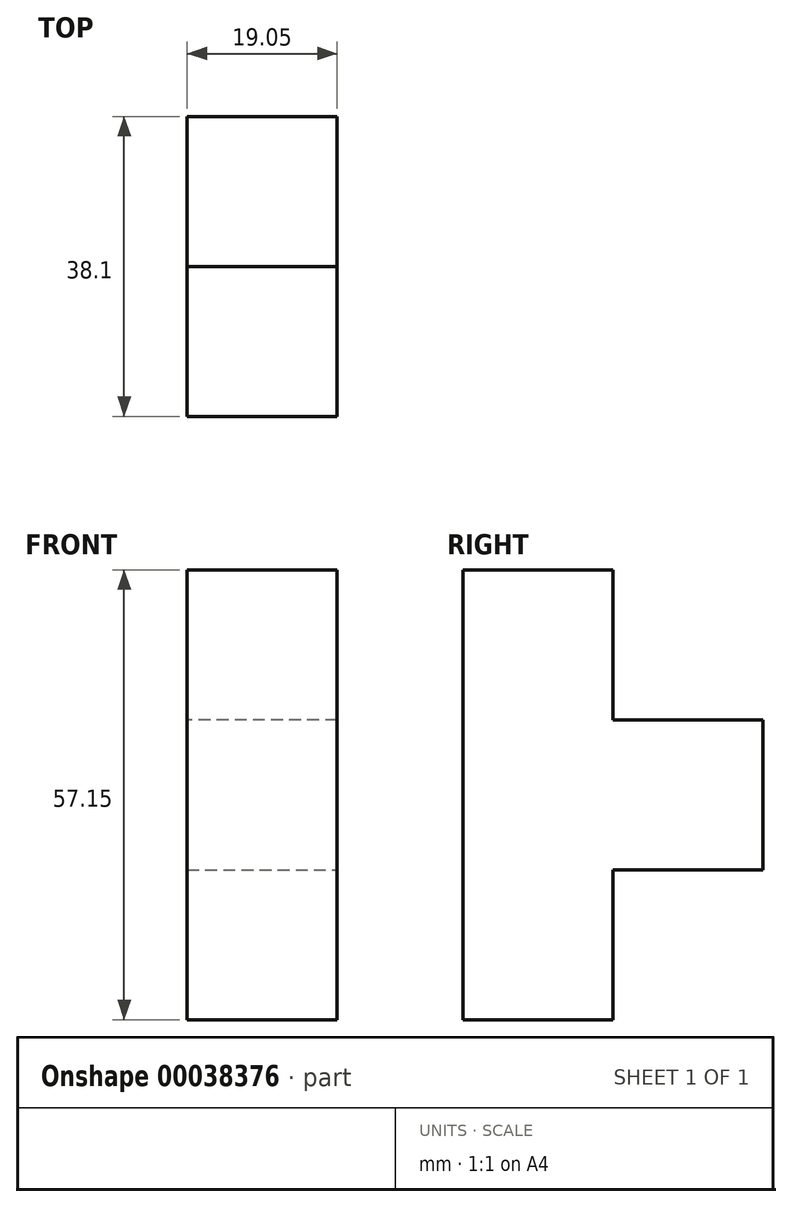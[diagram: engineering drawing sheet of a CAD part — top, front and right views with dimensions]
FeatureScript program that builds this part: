
annotation { "Feature Type Name" : "Feature", "Feature Type Description" : "" }
export const myFeature = defineFeature(function(context is Context, id is Id, definition is map)
    precondition{}
    {
        {
            var Q0;
            Q0=qCreatedBy(makeId("Top.planeOp"),FACE);
            var sketch = newSketch(context, id + "F0", { "sketchPlane" : qUnion([Q0])});
            skLineSegment(sketch, "E0.bottom", {"start": v(0, 0) * mm, "end": v(19.05, 0) * mm});
            skLineSegment(sketch, "E0.top", {"start": v(0, 19.05) * mm, "end": v(19.05, 19.05) * mm});
            skLineSegment(sketch, "E0.left", {"start": v(0, 0) * mm, "end": v(0, 19.05) * mm});
            skLineSegment(sketch, "E0.right", {"start": v(19.05, 0) * mm, "end": v(19.05, 19.05) * mm});
            skSolve(sketch);
        }
        {
            var Q0;
            Q0=makeQuery(id+"F0.imprint","IMPRINT",FACE,{"disambiguationData":[TD([[makeQuery(id+"F0.imprint","IMPRINT",EDGE,{"derivedFrom":sQuery(id+"F0.wireOp",EDGE,"E0.bottom")}),1.0]])]});
            extrude(context, id + "F1", {"entities" : qUnion([Q0]), "depth" : 19.05 * mm});
        }
        {
            var Q0;
            Q0=makeQuery(id+"F1.opExtrude","CAP_FACE",FACE,{"disambiguationData":[OSD([sQuery(id+"F0.wireOp",EDGE,"E0.bottom"),sQuery(id+"F0.wireOp",EDGE,"E0.top"),sQuery(id+"F0.wireOp",EDGE,"E0.left"),sQuery(id+"F0.wireOp",EDGE,"E0.right")])],"isStart":false});
            extrude(context, id + "F2", {"entities" : qUnion([Q0]), "operationType" : NewBodyOperationType.ADD, "depth" : 19.05 * mm});
        }
        {
            var Q0;
            {var subQ0=sQuery(id+"F0.wireOp",EDGE,"E0.top");Q0=makeQuery(id+"F2.boolean.opBoolean","MERGE",FACE,{"derivedFrom":[makeQuery(id+"F1.opExtrude","SWEPT_FACE",FACE,{"disambiguationData":[OSD([subQ0])]}),makeQuery(id+"F2.opExtrude","SWEPT_FACE",FACE,{"disambiguationData":[OSD([subQ0])]})]});}
            var sketch = newSketch(context, id + "F3", { "sketchPlane" : qUnion([Q0])});
            skLineSegment(sketch, "E1.bottom", {"start": v(0, 19.05) * mm, "end": v(-19.05, 19.05) * mm});
            skLineSegment(sketch, "E1.top", {"start": v(0, 38.1) * mm, "end": v(-19.05, 38.1) * mm});
            skLineSegment(sketch, "E1.left", {"start": v(0, 19.05) * mm, "end": v(0, 38.1) * mm});
            skLineSegment(sketch, "E1.right", {"start": v(-19.05, 19.05) * mm, "end": v(-19.05, 38.1) * mm});
            skSolve(sketch);
        }
        {
            var Q0;
            Q0=makeQuery(id+"F3.imprint","IMPRINT",FACE,{"disambiguationData":[TD([[makeQuery(id+"F3.imprint","IMPRINT",EDGE,{"derivedFrom":sQuery(id+"F3.wireOp",EDGE,"E1.bottom")}),-1.0]])]});
            extrude(context, id + "F4", {"entities" : qUnion([Q0]), "operationType" : NewBodyOperationType.ADD, "depth" : 19.05 * mm});
        }
        {
            var Q0;
            Q0=makeQuery(id+"F4.boolean.opBoolean","MERGE",FACE,{"derivedFrom":[makeQuery(id+"F2.opExtrude","CAP_FACE",FACE,{"disambiguationData":[OSD([sQuery(id+"F0.wireOp",EDGE,"E0.bottom"),sQuery(id+"F0.wireOp",EDGE,"E0.top"),sQuery(id+"F0.wireOp",EDGE,"E0.left"),sQuery(id+"F0.wireOp",EDGE,"E0.right")])],"isStart":false}),makeQuery(id+"F4.opExtrude","SWEPT_FACE",FACE,{"disambiguationData":[OSD([sQuery(id+"F3.wireOp",EDGE,"E1.top")])]})]});
            var sketch = newSketch(context, id + "F5", { "sketchPlane" : qUnion([Q0])});
            skLineSegment(sketch, "E2.bottom", {"start": v(19.05, 19.05) * mm, "end": v(0, 19.05) * mm});
            skLineSegment(sketch, "E2.top", {"start": v(19.05, 0) * mm, "end": v(0, 0) * mm});
            skLineSegment(sketch, "E2.left", {"start": v(19.05, 19.05) * mm, "end": v(19.05, 0) * mm});
            skLineSegment(sketch, "E2.right", {"start": v(0, 19.05) * mm, "end": v(0, 0) * mm});
            skSolve(sketch);
        }
        {
            var Q0;
            Q0=makeQuery(id+"F5.imprint","IMPRINT",FACE,{"disambiguationData":[TD([[makeQuery(id+"F5.imprint","IMPRINT",EDGE,{"derivedFrom":sQuery(id+"F5.wireOp",EDGE,"E2.bottom")}),1.0]])]});
            extrude(context, id + "F6", {"entities" : qUnion([Q0]), "operationType" : NewBodyOperationType.ADD, "depth" : 19.05 * mm});
        }
    });
